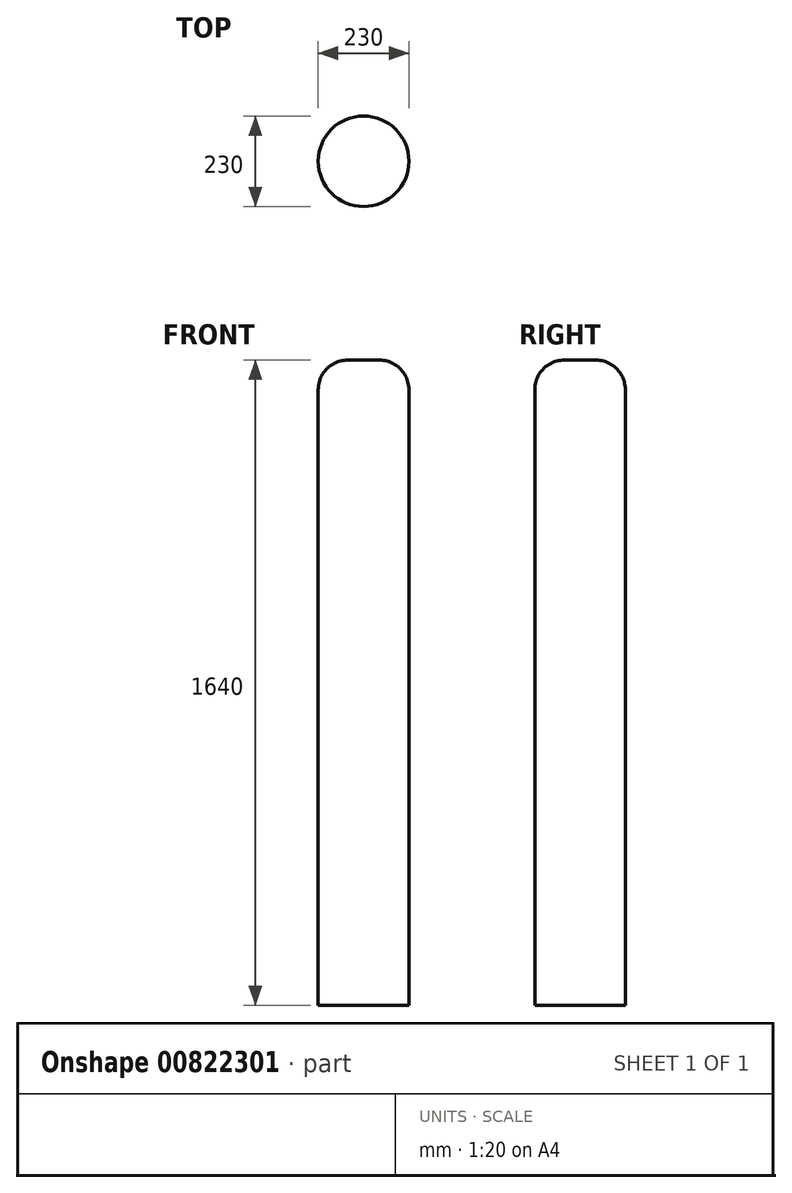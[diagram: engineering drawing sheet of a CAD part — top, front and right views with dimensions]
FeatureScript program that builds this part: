
annotation { "Feature Type Name" : "Feature", "Feature Type Description" : "" }
export const myFeature = defineFeature(function(context is Context, id is Id, definition is map)
    precondition{}
    {
        {
            var Q0;
            Q0=qCreatedBy(makeId("Top.planeOp"),FACE);
            var sketch = newSketch(context, id + "F0", { "sketchPlane" : qUnion([Q0])});
            skCircle(sketch, "E0", {"center": v(0, 0) * mm, "radius": 115 * mm});
            skSolve(sketch);
        }
        {
            var Q0;
            Q0 = qSketchRegion(id + "F0", true);
            extrude(context, id + "F1", {"entities" : qUnion([Q0]), "depth" : 1640 * mm, "offsetDistance" : 25 * mm});
        }
        {
            var Q0;
            Q0=makeQuery(id+"F1.opExtrude","CAP_FACE",FACE,{"disambiguationData":[OSD([sQuery(id+"F0.wireOp",EDGE,"E0")])],"isStart":false});
            fillet(context, id + "F2", {"entities" : qUnion([Q0]), "tangentPropagation" : true, "radius" : 75 * mm, "defaultsChanged" : true, "vertexSettings" : [], "allowEdgeOverflow" : false});
        }
    });
